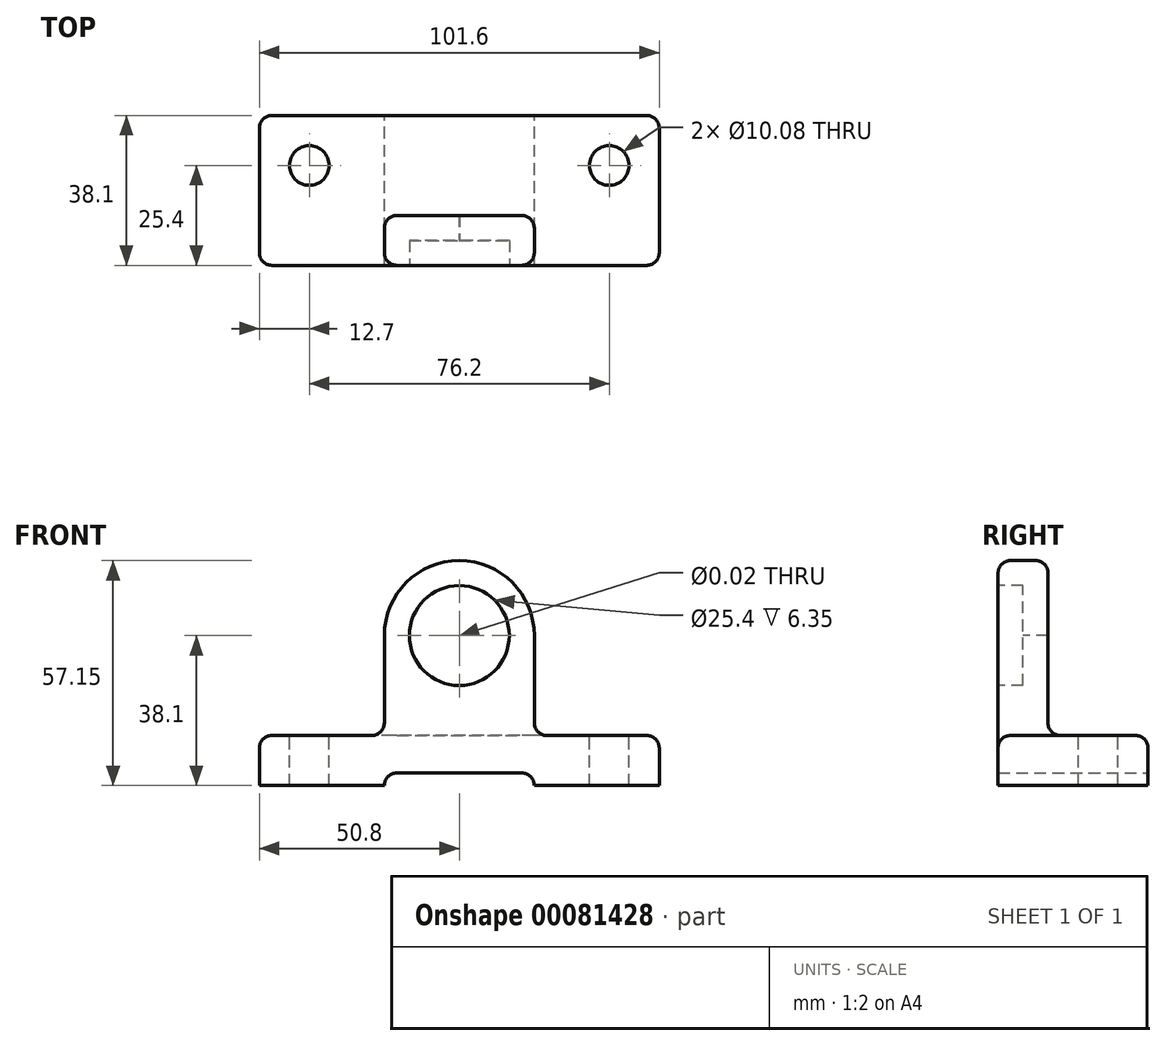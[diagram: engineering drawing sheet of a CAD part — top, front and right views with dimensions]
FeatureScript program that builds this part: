
annotation { "Feature Type Name" : "Feature", "Feature Type Description" : "" }
export const myFeature = defineFeature(function(context is Context, id is Id, definition is map)
    precondition{}
    {
        {
            var Q0;
            Q0=qCreatedBy(makeId("Top.planeOp"),FACE);
            var sketch = newSketch(context, id + "F0", { "sketchPlane" : qUnion([Q0])});
            skLineSegment(sketch, "E0.bottom", {"start": v(50.8, -19.05) * mm, "end": v(-50.8, -19.05) * mm});
            skLineSegment(sketch, "E0.top", {"start": v(50.8, 19.05) * mm, "end": v(-50.8, 19.05) * mm});
            skLineSegment(sketch, "E0.left", {"start": v(50.8, -19.05) * mm, "end": v(50.8, 19.05) * mm});
            skLineSegment(sketch, "E0.right", {"start": v(-50.8, -19.05) * mm, "end": v(-50.8, 19.05) * mm});
            skPoint(sketch, "E0.middle", {"position": v(0, 0) * mm});
            skSolve(sketch);
        }
        {
            var Q0;
            Q0=makeQuery(id+"F0.imprint","IMPRINT",FACE,{"disambiguationData":[TD([[makeQuery(id+"F0.imprint","IMPRINT",EDGE,{"derivedFrom":sQuery(id+"F0.wireOp",EDGE,"E0.bottom")}),-1.0]])]});
            extrude(context, id + "F1", {"entities" : qUnion([Q0]), "depth" : 12.7 * mm});
        }
        {
            var Q0;
            Q0=makeQuery(id+"F1.opExtrude","SWEPT_FACE",FACE,{"disambiguationData":[OSD([sQuery(id+"F0.wireOp",EDGE,"E0.bottom")])]});
            var sketch = newSketch(context, id + "F2", { "sketchPlane" : qUnion([Q0])});
            skLineSegment(sketch, "E1", {"start": v(-19.05, 0) * mm, "end": v(-19.05, 38.1) * mm});
            skArc(sketch, "E2", {"start": v(-19.05, 38.1) * mm, "mid": v(0, 57.15) * mm, "end": v(19.05, 38.1) * mm});
            skLineSegment(sketch, "E3", {"start": v(19.05, 38.1) * mm, "end": v(19.05, 0) * mm});
            skLineSegment(sketch, "E4", {"start": v(19.05, 0) * mm, "end": v(-19.05, 0) * mm});
            skPoint(sketch, "E5.endSnap0", {"position": v(0, 0) * mm});
            skLineSegment(sketch, "E6", {"start": v(0, 69.34) * mm, "end": v(0, 12.7) * mm, "construction": true});
            skPoint(sketch, "E6.startSnap0", {"position": v(0, 57.15) * mm});
            skSolve(sketch);
        }
        {
            var Q0;
            Q0 = qSketchRegion(id + "F2", true);
            extrude(context, id + "F3", {"entities" : qUnion([Q0]), "operationType" : NewBodyOperationType.ADD, "oppositeDirection" : true, "depth" : 12.7 * mm});
        }
        {
            var Q0;
            Q0=sQuery(id+"F2.wireOp",VERTEX,"E2.center");
            var Q1;
            Q1=makeQuery(id+"F1.opExtrude","SWEPT_BODY",BODY,{"disambiguationData":[OSD([sQuery(id+"F0.wireOp",EDGE,"E0.bottom"),sQuery(id+"F0.wireOp",EDGE,"E0.top"),sQuery(id+"F0.wireOp",EDGE,"E0.left"),sQuery(id+"F0.wireOp",EDGE,"E0.right")])]});
            hole(context, id + "F4", {"style" : HoleStyle.C_BORE, "endStyle" : HoleEndStyle.THROUGH, "standardTappedOrClearance" : lookupTablePath({ "standard" : "ANSI", "size" : "15/32 (0.47)", "type" : "Drilled" }), "standardBlindInLast" : lookupTablePath({ "standard" : "ANSI", "size" : "15/32", "type" : "Drilled" }), "holeDiameter" : 15 / 812.8 * mm, "cBoreDiameter" : 25.4 * mm, "cBoreDepth" : 6.35 * mm, "locations" : qUnion([Q0]), "scope" : qUnion([Q1]), "isTappedThrough" : true});
        }
        {
            var Q0;
            Q0=makeQuery(id+"F1.opExtrude","SWEPT_FACE",FACE,{"disambiguationData":[OSD([sQuery(id+"F0.wireOp",EDGE,"E0.top")])]});
            var sketch = newSketch(context, id + "F5", { "sketchPlane" : qUnion([Q0])});
            skLineSegment(sketch, "E7", {"start": v(-19.05, 0) * mm, "end": v(-19.05, 3.18) * mm});
            skLineSegment(sketch, "E8", {"start": v(-19.05, 3.18) * mm, "end": v(19.05, 3.18) * mm});
            skLineSegment(sketch, "E9", {"start": v(19.05, 3.18) * mm, "end": v(19.05, 0) * mm});
            skLineSegment(sketch, "E10", {"start": v(19.05, 0) * mm, "end": v(-19.05, 0) * mm});
            skSolve(sketch);
        }
        {
            var Q0;
            Q0=makeQuery(id+"F5.imprint","IMPRINT",FACE,{"disambiguationData":[TD([[makeQuery(id+"F5.imprint","IMPRINT",EDGE,{"derivedFrom":sQuery(id+"F5.wireOp",EDGE,"E7")}),-1.0]])]});
            extrude(context, id + "F6", {"entities" : qUnion([Q0]), "operationType" : NewBodyOperationType.REMOVE, "endBound" : BoundingType.THROUGH_ALL, "oppositeDirection" : true, "depth" : 25.4 * mm});
        }
        {
            var Q0;
            Q0=makeQuery(id+"F1.opExtrude","CAP_FACE",FACE,{"disambiguationData":[OSD([sQuery(id+"F0.wireOp",EDGE,"E0.bottom"),sQuery(id+"F0.wireOp",EDGE,"E0.top"),sQuery(id+"F0.wireOp",EDGE,"E0.left"),sQuery(id+"F0.wireOp",EDGE,"E0.right")])],"isStart":false});
            var sketch = newSketch(context, id + "F7", { "sketchPlane" : qUnion([Q0])});
            skPoint(sketch, "E11", {"position": v(-50.8, 19.05) * mm});
            skPoint(sketch, "E12", {"position": v(-50.8, 6.35) * mm});
            skPoint(sketch, "E13", {"position": v(-38.1, 6.35) * mm});
            skPoint(sketch, "E14", {"position": v(50.8, 6.35) * mm});
            skPoint(sketch, "E15", {"position": v(38.1, 6.35) * mm});
            skPoint(sketch, "E16", {"position": v(50.8, 19.05) * mm});
            skSolve(sketch);
        }
        {
            var Q0;
            Q0=sQuery(id+"F7.wireOp",VERTEX,"E13");
            var Q1;
            Q1=sQuery(id+"F7.wireOp",VERTEX,"E15");
            var Q2;
            Q2=makeQuery(id+"F1.opExtrude","SWEPT_BODY",BODY,{"disambiguationData":[OSD([sQuery(id+"F0.wireOp",EDGE,"E0.bottom"),sQuery(id+"F0.wireOp",EDGE,"E0.top"),sQuery(id+"F0.wireOp",EDGE,"E0.left"),sQuery(id+"F0.wireOp",EDGE,"E0.right")])]});
            hole(context, id + "F8", {"style" : HoleStyle.SIMPLE, "endStyle" : HoleEndStyle.THROUGH, "standardTappedOrClearance" : lookupTablePath({ "standard" : "ANSI", "fit" : "Normal (ASME)", "size" : "3/8", "type" : "Clearance" }), "standardBlindInLast" : lookupTablePath({ "fit" : "Free", "standard" : "ANSI", "size" : "3/8", "type" : "Clearance" }), "holeDiameter" : 10.08 * mm, "locations" : qUnion([Q0, Q1]), "scope" : qUnion([Q2]), "isTappedThrough" : true});
        }
        {
            var Q0;
            Q0=makeQuery(id+"F1.opExtrude","SWEPT_EDGE",EDGE,{"disambiguationData":[OSD([sQuery(id+"F0.wireOp",EDGE,"E0.bottom"),sQuery(id+"F0.wireOp",EDGE,"E0.right")])]});
            fillet(context, id + "F9", {"entities" : qUnion([Q0]), "radius" : 3.17 * mm, "tangentPropagation" : true, "allowEdgeOverflow" : false});
        }
        {
            var Q0;
            Q0=makeQuery(id+"F1.opExtrude","SWEPT_EDGE",EDGE,{"disambiguationData":[OSD([sQuery(id+"F0.wireOp",EDGE,"E0.top"),sQuery(id+"F0.wireOp",EDGE,"E0.right")])]});
            var Q1;
            Q1=makeQuery(id+"F1.opExtrude","SWEPT_EDGE",EDGE,{"disambiguationData":[OSD([sQuery(id+"F0.wireOp",EDGE,"E0.bottom"),sQuery(id+"F0.wireOp",EDGE,"E0.left")])]});
            fillet(context, id + "F10", {"entities" : qUnion([Q0, Q1]), "radius" : 3.17 * mm, "tangentPropagation" : true, "allowEdgeOverflow" : false});
        }
        {
            var Q0;
            Q0=makeQuery(id+"F1.opExtrude","SWEPT_EDGE",EDGE,{"disambiguationData":[OSD([sQuery(id+"F0.wireOp",EDGE,"E0.top"),sQuery(id+"F0.wireOp",EDGE,"E0.left")])]});
            fillet(context, id + "F11", {"entities" : qUnion([Q0]), "radius" : 3.17 * mm, "tangentPropagation" : true, "allowEdgeOverflow" : false});
        }
        {
            var Q0;
            Q0=makeQuery(id+"F6.boolean.opBoolean","COPY",EDGE,{"derivedFrom":makeQuery(id+"F6.opExtrude","SWEPT_EDGE",EDGE,{"disambiguationData":[OSD([sQuery(id+"F5.wireOp",EDGE,"E8"),sQuery(id+"F5.wireOp",EDGE,"E9")])]})});
            var Q1;
            Q1=makeQuery(id+"F6.boolean.opBoolean","COPY",EDGE,{"derivedFrom":makeQuery(id+"F6.opExtrude","SWEPT_EDGE",EDGE,{"disambiguationData":[OSD([sQuery(id+"F5.wireOp",EDGE,"E7"),sQuery(id+"F5.wireOp",EDGE,"E8")])]})});
            fillet(context, id + "F12", {"entities" : qUnion([Q0, Q1]), "radius" : 3.17 * mm, "tangentPropagation" : true, "allowEdgeOverflow" : false});
        }
        {
            var Q0;
            Q0=makeQuery(id+"F3.opExtrude","CAP_EDGE",EDGE,{"disambiguationData":[OSD([sQuery(id+"F2.wireOp",EDGE,"E2")])],"isStart":true});
            var Q1;
            Q1=makeQuery(id+"F3.opExtrude","CAP_EDGE",EDGE,{"disambiguationData":[OSD([sQuery(id+"F2.wireOp",EDGE,"E3")])],"isStart":true});
            var Q2;
            Q2=makeQuery(id+"F3.opExtrude","CAP_EDGE",EDGE,{"disambiguationData":[OSD([sQuery(id+"F2.wireOp",EDGE,"E1")])],"isStart":true});
            var Q3;
            {var subQ0=sQuery(id+"F0.wireOp",EDGE,"E0.right");var subQ2=sQuery(id+"F0.wireOp",EDGE,"E0.bottom");Q3=makeQuery(id+"F3.boolean.opBoolean","SPLIT",EDGE,{"disambiguationData":[TD([makeQuery(id+"F1.opExtrude","SWEPT_FACE",FACE,{"disambiguationData":[OSD([subQ0])]})])],"derivedFrom":makeQuery(id+"F1.opExtrude","CAP_EDGE",EDGE,{"disambiguationData":[OSD([subQ2])],"isStart":false})});}
            var Q4;
            {var subQ0=sQuery(id+"F0.wireOp",EDGE,"E0.left");var subQ2=sQuery(id+"F0.wireOp",EDGE,"E0.bottom");Q4=makeQuery(id+"F3.boolean.opBoolean","SPLIT",EDGE,{"disambiguationData":[TD([makeQuery(id+"F1.opExtrude","SWEPT_FACE",FACE,{"disambiguationData":[OSD([subQ0])]})])],"derivedFrom":makeQuery(id+"F1.opExtrude","CAP_EDGE",EDGE,{"disambiguationData":[OSD([subQ2])],"isStart":false})});}
            var Q5;
            {var subQ0=sQuery(id+"F0.wireOp",EDGE,"E0.left");var subQ1=sQuery(id+"F0.wireOp",EDGE,"E0.bottom");Q5=makeQuery(id+"F10.opFillet","BLEND_EDGE",EDGE,{"blendedFrom":[makeQuery(id+"F1.opExtrude","SWEPT_EDGE",EDGE,{"disambiguationData":[OSD([subQ1,subQ0])]}),makeQuery(id+"F1.opExtrude","CAP_FACE",FACE,{"disambiguationData":[OSD([subQ1,sQuery(id+"F0.wireOp",EDGE,"E0.top"),subQ0,sQuery(id+"F0.wireOp",EDGE,"E0.right")])],"isStart":false})],"blendedInto":[makeQuery(id+"F1.opExtrude","CAP_FACE",FACE,{"disambiguationData":[OSD([subQ1,sQuery(id+"F0.wireOp",EDGE,"E0.top"),subQ0,sQuery(id+"F0.wireOp",EDGE,"E0.right")])],"isStart":false})]});}
            var Q6;
            Q6=makeQuery(id+"F1.opExtrude","CAP_EDGE",EDGE,{"disambiguationData":[OSD([sQuery(id+"F0.wireOp",EDGE,"E0.left")])],"isStart":false});
            var Q7;
            Q7=makeQuery(id+"F1.opExtrude","CAP_EDGE",EDGE,{"disambiguationData":[OSD([sQuery(id+"F0.wireOp",EDGE,"E0.top")])],"isStart":false});
            var Q8;
            {var subQ0=sQuery(id+"F0.wireOp",EDGE,"E0.left");var subQ1=sQuery(id+"F0.wireOp",EDGE,"E0.top");Q8=makeQuery(id+"F11.opFillet","BLEND_EDGE",EDGE,{"blendedFrom":[makeQuery(id+"F1.opExtrude","SWEPT_EDGE",EDGE,{"disambiguationData":[OSD([subQ1,subQ0])]}),makeQuery(id+"F1.opExtrude","CAP_FACE",FACE,{"disambiguationData":[OSD([sQuery(id+"F0.wireOp",EDGE,"E0.bottom"),subQ1,subQ0,sQuery(id+"F0.wireOp",EDGE,"E0.right")])],"isStart":false})],"blendedInto":[makeQuery(id+"F1.opExtrude","CAP_FACE",FACE,{"disambiguationData":[OSD([sQuery(id+"F0.wireOp",EDGE,"E0.bottom"),subQ1,subQ0,sQuery(id+"F0.wireOp",EDGE,"E0.right")])],"isStart":false})]});}
            var Q9;
            {var subQ0=sQuery(id+"F0.wireOp",EDGE,"E0.right");var subQ1=sQuery(id+"F0.wireOp",EDGE,"E0.top");Q9=makeQuery(id+"F10.opFillet","BLEND_EDGE",EDGE,{"blendedFrom":[makeQuery(id+"F1.opExtrude","SWEPT_EDGE",EDGE,{"disambiguationData":[OSD([subQ1,subQ0])]}),makeQuery(id+"F1.opExtrude","CAP_FACE",FACE,{"disambiguationData":[OSD([sQuery(id+"F0.wireOp",EDGE,"E0.bottom"),subQ1,sQuery(id+"F0.wireOp",EDGE,"E0.left"),subQ0])],"isStart":false})],"blendedInto":[makeQuery(id+"F1.opExtrude","CAP_FACE",FACE,{"disambiguationData":[OSD([sQuery(id+"F0.wireOp",EDGE,"E0.bottom"),subQ1,sQuery(id+"F0.wireOp",EDGE,"E0.left"),subQ0])],"isStart":false})]});}
            var Q10;
            Q10=makeQuery(id+"F1.opExtrude","CAP_EDGE",EDGE,{"disambiguationData":[OSD([sQuery(id+"F0.wireOp",EDGE,"E0.right")])],"isStart":false});
            var Q11;
            {var subQ0=sQuery(id+"F0.wireOp",EDGE,"E0.right");var subQ1=sQuery(id+"F0.wireOp",EDGE,"E0.bottom");Q11=makeQuery(id+"F9.opFillet","BLEND_EDGE",EDGE,{"blendedFrom":[makeQuery(id+"F1.opExtrude","SWEPT_EDGE",EDGE,{"disambiguationData":[OSD([subQ1,subQ0])]}),makeQuery(id+"F1.opExtrude","CAP_FACE",FACE,{"disambiguationData":[OSD([subQ1,sQuery(id+"F0.wireOp",EDGE,"E0.top"),sQuery(id+"F0.wireOp",EDGE,"E0.left"),subQ0])],"isStart":false})],"blendedInto":[makeQuery(id+"F1.opExtrude","CAP_FACE",FACE,{"disambiguationData":[OSD([subQ1,sQuery(id+"F0.wireOp",EDGE,"E0.top"),sQuery(id+"F0.wireOp",EDGE,"E0.left"),subQ0])],"isStart":false})]});}
            var Q12;
            Q12=makeQuery(id+"F3.boolean.opBoolean","INTERSECT",EDGE,{"derivedFrom":[makeQuery(id+"F1.opExtrude","CAP_FACE",FACE,{"disambiguationData":[OSD([sQuery(id+"F0.wireOp",EDGE,"E0.bottom"),sQuery(id+"F0.wireOp",EDGE,"E0.top"),sQuery(id+"F0.wireOp",EDGE,"E0.left"),sQuery(id+"F0.wireOp",EDGE,"E0.right")])],"isStart":false}),makeQuery(id+"F3.opExtrude","SWEPT_FACE",FACE,{"disambiguationData":[OSD([sQuery(id+"F2.wireOp",EDGE,"E3")])]})]});
            var Q13;
            Q13=makeQuery(id+"F3.opExtrude","CAP_EDGE",EDGE,{"disambiguationData":[OSD([sQuery(id+"F2.wireOp",EDGE,"E3")])],"isStart":false});
            var Q14;
            Q14=makeQuery(id+"F3.opExtrude","CAP_EDGE",EDGE,{"disambiguationData":[OSD([sQuery(id+"F2.wireOp",EDGE,"E2")])],"isStart":false});
            var Q15;
            Q15=makeQuery(id+"F3.opExtrude","CAP_EDGE",EDGE,{"disambiguationData":[OSD([sQuery(id+"F2.wireOp",EDGE,"E1")])],"isStart":false});
            var Q16;
            Q16=makeQuery(id+"F3.boolean.opBoolean","INTERSECT",EDGE,{"derivedFrom":[makeQuery(id+"F1.opExtrude","CAP_FACE",FACE,{"disambiguationData":[OSD([sQuery(id+"F0.wireOp",EDGE,"E0.bottom"),sQuery(id+"F0.wireOp",EDGE,"E0.top"),sQuery(id+"F0.wireOp",EDGE,"E0.left"),sQuery(id+"F0.wireOp",EDGE,"E0.right")])],"isStart":false}),makeQuery(id+"F3.opExtrude","SWEPT_FACE",FACE,{"disambiguationData":[OSD([sQuery(id+"F2.wireOp",EDGE,"E1")])]})]});
            var Q17;
            Q17=makeQuery(id+"F3.boolean.opBoolean","INTERSECT",EDGE,{"derivedFrom":[makeQuery(id+"F1.opExtrude","CAP_FACE",FACE,{"disambiguationData":[OSD([sQuery(id+"F0.wireOp",EDGE,"E0.bottom"),sQuery(id+"F0.wireOp",EDGE,"E0.top"),sQuery(id+"F0.wireOp",EDGE,"E0.left"),sQuery(id+"F0.wireOp",EDGE,"E0.right")])],"isStart":false}),makeQuery(id+"F3.opExtrude","CAP_FACE",FACE,{"disambiguationData":[OSD([sQuery(id+"F2.wireOp",EDGE,"E1"),sQuery(id+"F2.wireOp",EDGE,"E2"),sQuery(id+"F2.wireOp",EDGE,"E3"),sQuery(id+"F2.wireOp",EDGE,"E4")])],"isStart":false})]});
            fillet(context, id + "F13", {"entities" : qUnion([Q0, Q1, Q2, Q3, Q4, Q5, Q6, Q7, Q8, Q9, Q10, Q11, Q12, Q13, Q14, Q15, Q16, Q17]), "radius" : 3.17 * mm, "tangentPropagation" : true, "allowEdgeOverflow" : false});
        }
    });
